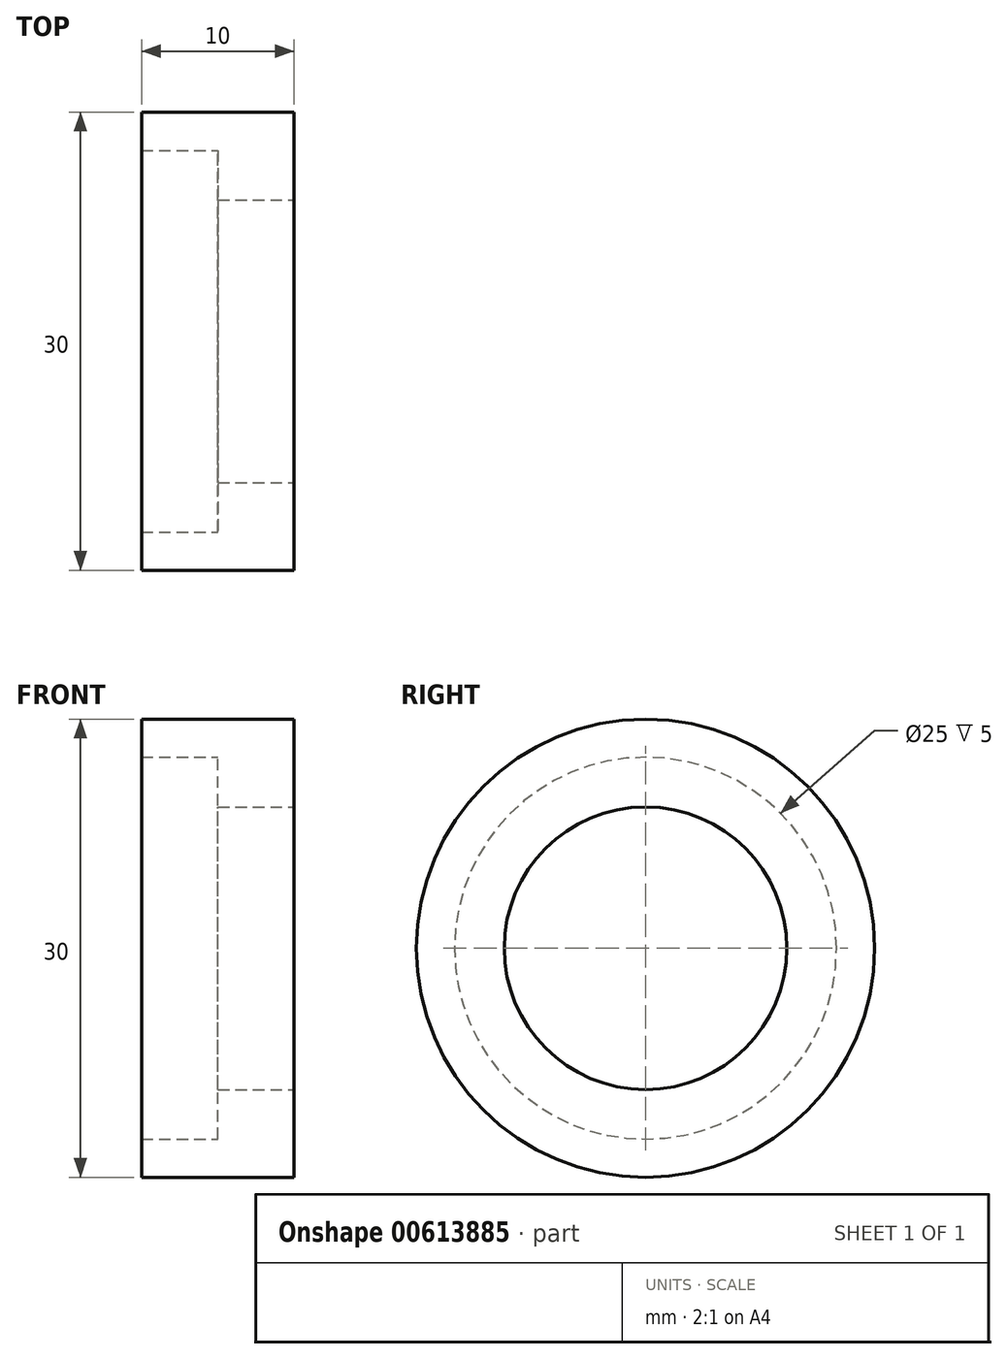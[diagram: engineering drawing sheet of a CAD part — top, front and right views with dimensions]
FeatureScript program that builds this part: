
annotation { "Feature Type Name" : "Feature", "Feature Type Description" : "" }
export const myFeature = defineFeature(function(context is Context, id is Id, definition is map)
    precondition{}
    {
        {
            var Q0;
            Q0=qCreatedBy(makeId("Right.planeOp"),FACE);
            var sketch = newSketch(context, id + "F0", { "sketchPlane" : qUnion([Q0])});
            skCircle(sketch, "E0", {"center": v(0, 0) * mm, "radius": 9.25 * mm});
            skSolve(sketch);
        }
        {
            var Q0;
            Q0=qCreatedBy(makeId("Right.planeOp"),FACE);
            var sketch = newSketch(context, id + "F1", { "sketchPlane" : qUnion([Q0])});
            skCircle(sketch, "E1", {"center": v(0, 0) * mm, "radius": 15 * mm});
            skSolve(sketch);
        }
        {
            var Q0;
            Q0=makeQuery(id+"F1.imprint","IMPRINT",FACE,{"disambiguationData":[TD([[makeQuery(id+"F1.imprint","IMPRINT",EDGE,{"derivedFrom":sQuery(id+"F1.wireOp",EDGE,"E1")}),1.0]])]});
            extrude(context, id + "F2", {"entities" : qUnion([Q0]), "oppositeDirection" : true, "depth" : 10 * mm, "offsetDistance" : 25 * mm});
        }
        {
            var Q0;
            Q0=makeQuery(id+"F0.imprint","IMPRINT",FACE,{"disambiguationData":[TD([[makeQuery(id+"F0.imprint","IMPRINT",EDGE,{"derivedFrom":sQuery(id+"F0.wireOp",EDGE,"E0")}),1.0]])]});
            extrude(context, id + "F3", {"entities" : qUnion([Q0]), "operationType" : NewBodyOperationType.REMOVE, "oppositeDirection" : true, "depth" : 5 * mm, "offsetDistance" : 25 * mm});
        }
        {
            var Q0;
            Q0=makeQuery(id+"F3.boolean.opBoolean","COPY",FACE,{"derivedFrom":makeQuery(id+"F3.opExtrude","CAP_FACE",FACE,{"disambiguationData":[OSD([sQuery(id+"F0.wireOp",EDGE,"E0")])],"isStart":false})});
            var sketch = newSketch(context, id + "F4", { "sketchPlane" : qUnion([Q0])});
            skCircle(sketch, "E2", {"center": v(0, 0) * mm, "radius": 12.5 * mm});
            skSolve(sketch);
        }
        {
            var Q0;
            Q0 = qSketchRegion(id + "F4", true);
            extrude(context, id + "F5", {"entities" : qUnion([Q0]), "operationType" : NewBodyOperationType.REMOVE, "oppositeDirection" : true, "depth" : 25 * mm, "offsetDistance" : 25 * mm});
        }
    });
